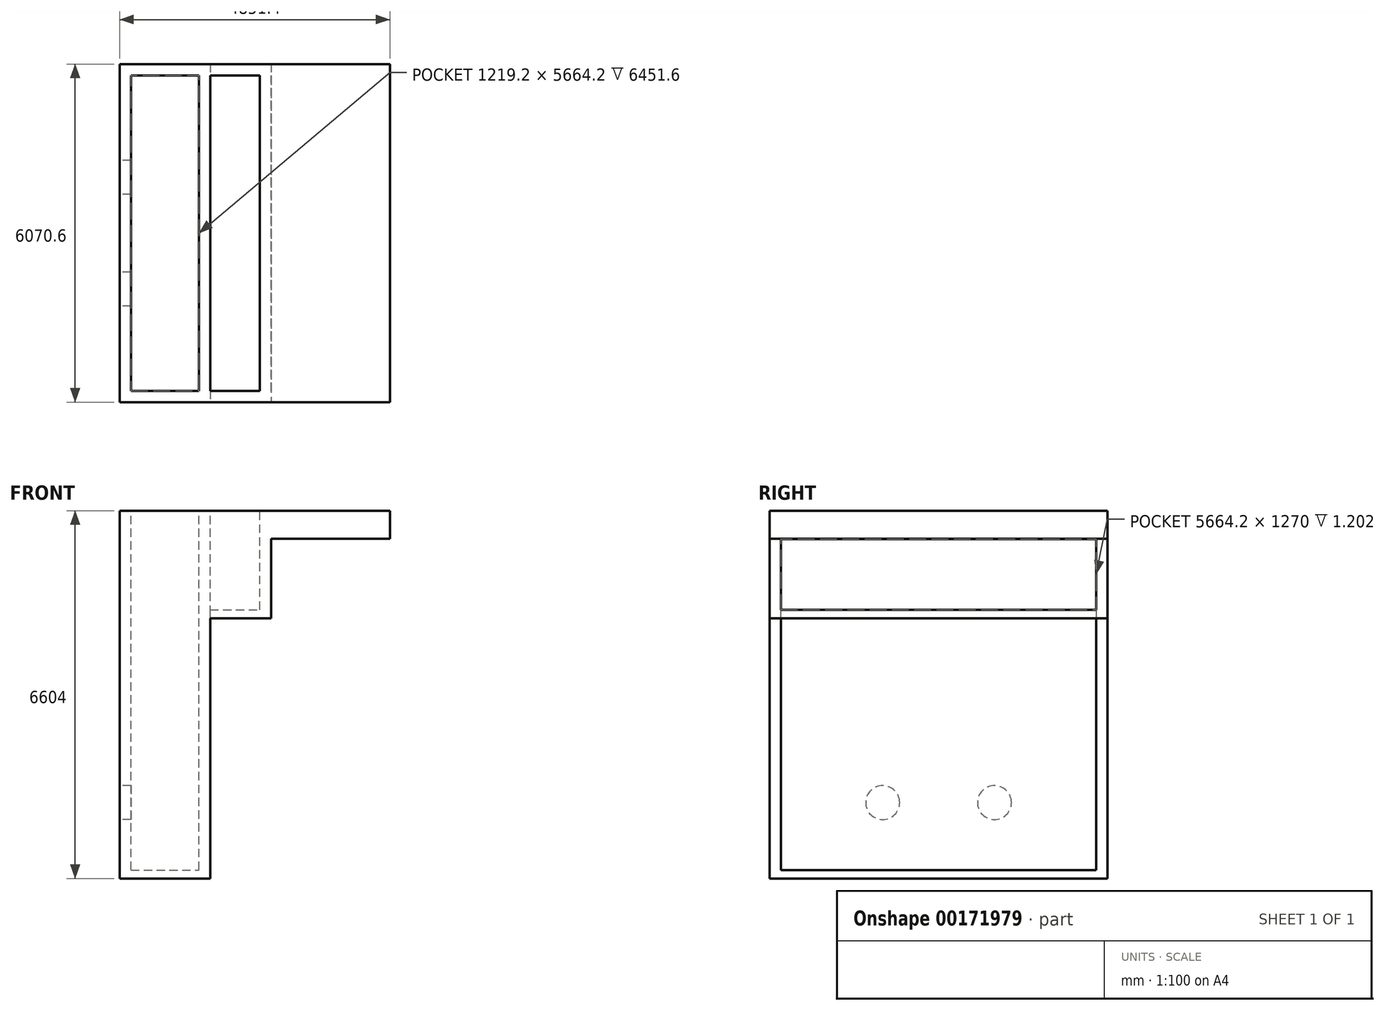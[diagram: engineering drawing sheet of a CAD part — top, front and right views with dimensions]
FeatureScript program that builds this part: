
annotation { "Feature Type Name" : "Feature", "Feature Type Description" : "" }
export const myFeature = defineFeature(function(context is Context, id is Id, definition is map)
    precondition{}
    {
        {
            var Q0;
            Q0=qCreatedBy(makeId("Top.planeOp"),FACE);
            var sketch = newSketch(context, id + "F0", { "sketchPlane" : qUnion([Q0])});
            skLineSegment(sketch, "E0.bottom", {"start": v(2222.5, 2832.1) * mm, "end": v(-2222.5, 2832.1) * mm});
            skLineSegment(sketch, "E0.top", {"start": v(2222.5, -2832.1) * mm, "end": v(-2222.5, -2832.1) * mm});
            skLineSegment(sketch, "E0.left", {"start": v(2222.5, 2832.1) * mm, "end": v(2222.5, -2832.1) * mm});
            skLineSegment(sketch, "E0.right", {"start": v(-2222.5, 2832.1) * mm, "end": v(-2222.5, -2832.1) * mm});
            skPoint(sketch, "E0.middle", {"position": v(0, 0) * mm});
            skSolve(sketch);
        }
        {
            var Q0;
            Q0=makeQuery(id+"F0.imprint","IMPRINT",FACE,{"disambiguationData":[TD([[makeQuery(id+"F0.imprint","IMPRINT",EDGE,{"derivedFrom":sQuery(id+"F0.wireOp",EDGE,"E0.bottom")}),1.0]])]});
            extrude(context, id + "F1", {"entities" : qUnion([Q0]), "oppositeDirection" : true, "depth" : 508 * mm});
        }
        {
            var Q0;
            Q0=makeQuery(id+"F1.opExtrude","CAP_FACE",FACE,{"disambiguationData":[OSD([sQuery(id+"F0.wireOp",EDGE,"E0.bottom"),sQuery(id+"F0.wireOp",EDGE,"E0.top"),sQuery(id+"F0.wireOp",EDGE,"E0.left"),sQuery(id+"F0.wireOp",EDGE,"E0.right")])],"isStart":true});
            var sketch = newSketch(context, id + "F2", { "sketchPlane" : qUnion([Q0])});
            skLineSegment(sketch, "E1.bottom", {"start": v(-2222.5, 2832.1) * mm, "end": v(-1003.3, 2832.1) * mm});
            skLineSegment(sketch, "E1.top", {"start": v(-2222.5, -2832.1) * mm, "end": v(-1003.3, -2832.1) * mm});
            skLineSegment(sketch, "E1.left", {"start": v(-2222.5, 2832.1) * mm, "end": v(-2222.5, -2832.1) * mm});
            skLineSegment(sketch, "E1.right", {"start": v(-1003.3, 2832.1) * mm, "end": v(-1003.3, -2832.1) * mm});
            skLineSegment(sketch, "E2.bottom", {"start": v(-1003.3, 2832.1) * mm, "end": v(-800.1, 2832.1) * mm});
            skLineSegment(sketch, "E2.top", {"start": v(-1003.3, -2832.1) * mm, "end": v(-800.1, -2832.1) * mm});
            skLineSegment(sketch, "E2.right", {"start": v(-800.1, 2832.1) * mm, "end": v(-800.1, -2832.1) * mm});
            skLineSegment(sketch, "E3.bottom", {"start": v(-800.1, 2832.1) * mm, "end": v(88.9, 2832.1) * mm});
            skLineSegment(sketch, "E3.top", {"start": v(-800.1, -2832.1) * mm, "end": v(88.9, -2832.1) * mm});
            skLineSegment(sketch, "E3.right", {"start": v(88.9, 2832.1) * mm, "end": v(88.9, -2832.1) * mm});
            skSolve(sketch);
        }
        {
            var Q0;
            Q0=makeQuery(id+"F2.imprint","IMPRINT",FACE,{"disambiguationData":[TD([[makeQuery(id+"F2.imprint","IMPRINT",EDGE,{"derivedFrom":sQuery(id+"F2.wireOp",EDGE,"E1.bottom")}),1.0]])]});
            var Q1;
            Q1=makeQuery(id+"F2.imprint","IMPRINT",FACE,{"disambiguationData":[TD([[makeQuery(id+"F2.imprint","IMPRINT",EDGE,{"derivedFrom":sQuery(id+"F2.wireOp",EDGE,"E3.bottom")}),1.0]])]});
            extrude(context, id + "F3", {"entities" : qUnion([Q0, Q1]), "operationType" : NewBodyOperationType.REMOVE, "oppositeDirection" : true, "depth" : 609.6 * mm});
        }
        {
            var Q0;
            Q0=makeQuery(id+"F1.opExtrude","CAP_FACE",FACE,{"disambiguationData":[OSD([sQuery(id+"F0.wireOp",EDGE,"E0.bottom"),sQuery(id+"F0.wireOp",EDGE,"E0.top"),sQuery(id+"F0.wireOp",EDGE,"E0.left"),sQuery(id+"F0.wireOp",EDGE,"E0.right")])],"isStart":false});
            var sketch = newSketch(context, id + "F4", { "sketchPlane" : qUnion([Q0])});
            skLineSegment(sketch, "E4.bottom", {"start": v(-2222.5, 2832.1) * mm, "end": v(2222.5, 2832.1) * mm});
            skLineSegment(sketch, "E4.top", {"start": v(-2222.5, -2832.1) * mm, "end": v(2222.5, -2832.1) * mm});
            skLineSegment(sketch, "E4.left", {"start": v(-2222.5, 2832.1) * mm, "end": v(-2222.5, -2832.1) * mm});
            skLineSegment(sketch, "E4.right", {"start": v(2222.5, 2832.1) * mm, "end": v(2222.5, -2832.1) * mm});
            skPoint(sketch, "E4.middle", {"position": v(0, 0) * mm});
            skLineSegment(sketch, "E5.bottom", {"start": v(-2425.7, 3035.3) * mm, "end": v(2425.7, 3035.3) * mm});
            skLineSegment(sketch, "E5.top", {"start": v(-2425.7, -3035.3) * mm, "end": v(2425.7, -3035.3) * mm});
            skLineSegment(sketch, "E5.left", {"start": v(-2425.7, 3035.3) * mm, "end": v(-2425.7, -3035.3) * mm});
            skLineSegment(sketch, "E5.right", {"start": v(2425.7, 3035.3) * mm, "end": v(2425.7, -3035.3) * mm});
            skSolve(sketch);
        }
        {
            var Q0;
            Q0 = qSketchRegion(id + "F4", true);
            extrude(context, id + "F5", {"entities" : qUnion([Q0]), "depth" : 6096 * mm});
        }
        {
            var Q0;
            Q0=makeQuery(id+"F5.opExtrude","CAP_FACE",FACE,{"disambiguationData":[OSD([sQuery(id+"F4.wireOp",EDGE,"E4.bottom"),sQuery(id+"F4.wireOp",EDGE,"E4.top"),sQuery(id+"F4.wireOp",EDGE,"E4.left"),sQuery(id+"F4.wireOp",EDGE,"E4.right"),sQuery(id+"F4.wireOp",EDGE,"E5.bottom"),sQuery(id+"F4.wireOp",EDGE,"E5.top"),sQuery(id+"F4.wireOp",EDGE,"E5.left"),sQuery(id+"F4.wireOp",EDGE,"E5.right")])],"isStart":true});
            extrude(context, id + "F6", {"entities" : qUnion([Q0]), "depth" : 508 * mm});
        }
        {
            var Q0;
            Q0=makeQuery(id+"F3.boolean.opBoolean","SPLIT",BODY,{"disambiguationData":[OD(0.0)],"derivedFrom":makeQuery(id+"F1.opExtrude","SWEPT_BODY",BODY,{"disambiguationData":[OSD([sQuery(id+"F0.wireOp",EDGE,"E0.bottom"),sQuery(id+"F0.wireOp",EDGE,"E0.top"),sQuery(id+"F0.wireOp",EDGE,"E0.left"),sQuery(id+"F0.wireOp",EDGE,"E0.right")])]})});
            var Q1;
            Q1=makeQuery(id+"F3.boolean.opBoolean","SPLIT",BODY,{"disambiguationData":[OD(1.0)],"derivedFrom":makeQuery(id+"F1.opExtrude","SWEPT_BODY",BODY,{"disambiguationData":[OSD([sQuery(id+"F0.wireOp",EDGE,"E0.bottom"),sQuery(id+"F0.wireOp",EDGE,"E0.top"),sQuery(id+"F0.wireOp",EDGE,"E0.left"),sQuery(id+"F0.wireOp",EDGE,"E0.right")])]})});
            var Q2;
            Q2=makeQuery(id+"F5.opExtrude","SWEPT_BODY",BODY,{"disambiguationData":[OSD([sQuery(id+"F4.wireOp",EDGE,"E4.bottom"),sQuery(id+"F4.wireOp",EDGE,"E4.top"),sQuery(id+"F4.wireOp",EDGE,"E4.left"),sQuery(id+"F4.wireOp",EDGE,"E4.right"),sQuery(id+"F4.wireOp",EDGE,"E5.bottom"),sQuery(id+"F4.wireOp",EDGE,"E5.top"),sQuery(id+"F4.wireOp",EDGE,"E5.left"),sQuery(id+"F4.wireOp",EDGE,"E5.right")])]});
            var Q3;
            Q3=makeQuery(id+"F6.opExtrude","SWEPT_BODY",BODY,{"disambiguationData":[OSD([sQuery(id+"F4.wireOp",EDGE,"E4.bottom"),sQuery(id+"F4.wireOp",EDGE,"E4.top"),sQuery(id+"F4.wireOp",EDGE,"E4.left"),sQuery(id+"F4.wireOp",EDGE,"E4.right"),sQuery(id+"F4.wireOp",EDGE,"E5.bottom"),sQuery(id+"F4.wireOp",EDGE,"E5.top"),sQuery(id+"F4.wireOp",EDGE,"E5.left"),sQuery(id+"F4.wireOp",EDGE,"E5.right")])]});
            booleanBodies(context, id + "F7", {"operationType" : BooleanOperationType.UNION, "tools" : qUnion([Q0, Q1, Q2, Q3])});
        }
        {
            var Q0;
            {var subQ0=sQuery(id+"F0.wireOp",EDGE,"E0.bottom");var subQ1=sQuery(id+"F0.wireOp",EDGE,"E0.top");Q0=makeQuery(id+"F3.boolean.opBoolean","SPLIT",FACE,{"disambiguationData":[TD([makeQuery(id+"F3.opExtrude","SWEPT_FACE",FACE,{"disambiguationData":[OSD([sQuery(id+"F2.wireOp",EDGE,"E1.right")])]})])],"derivedFrom":makeQuery(id+"F1.opExtrude","CAP_FACE",FACE,{"disambiguationData":[OSD([subQ0,subQ1,sQuery(id+"F0.wireOp",EDGE,"E0.left"),sQuery(id+"F0.wireOp",EDGE,"E0.right")])],"isStart":false})});}
            extrude(context, id + "F8", {"entities" : qUnion([Q0]), "operationType" : NewBodyOperationType.ADD, "depth" : 6096 * mm});
        }
        {
            var Q0;
            {var subQ0=sQuery(id+"F0.wireOp",EDGE,"E0.bottom");var subQ1=sQuery(id+"F0.wireOp",EDGE,"E0.top");var subQ2=sQuery(id+"F0.wireOp",EDGE,"E0.left");Q0=makeQuery(id+"F3.boolean.opBoolean","SPLIT",FACE,{"disambiguationData":[TD([makeQuery(id+"F1.opExtrude","SWEPT_FACE",FACE,{"disambiguationData":[OSD([subQ2])]})])],"derivedFrom":makeQuery(id+"F1.opExtrude","CAP_FACE",FACE,{"disambiguationData":[OSD([subQ0,subQ1,subQ2,sQuery(id+"F0.wireOp",EDGE,"E0.right")])],"isStart":false})});}
            var sketch = newSketch(context, id + "F9", { "sketchPlane" : qUnion([Q0])});
            skLineSegment(sketch, "E6.bottom", {"start": v(88.9, 2832.1) * mm, "end": v(292.1, 2832.1) * mm});
            skLineSegment(sketch, "E6.top", {"start": v(88.9, -2832.1) * mm, "end": v(292.1, -2832.1) * mm});
            skLineSegment(sketch, "E6.left", {"start": v(88.9, 2832.1) * mm, "end": v(88.9, -2832.1) * mm});
            skLineSegment(sketch, "E6.right", {"start": v(292.1, 2832.1) * mm, "end": v(292.1, -2832.1) * mm});
            skSolve(sketch);
        }
        {
            var Q0;
            Q0 = qSketchRegion(id + "F9", true);
            extrude(context, id + "F10", {"entities" : qUnion([Q0]), "operationType" : NewBodyOperationType.ADD, "depth" : 6096 * mm});
        }
        {
            var Q0;
            {var subQ0=sQuery(id+"F4.wireOp",EDGE,"E5.left");Q0=makeQuery(id+"F7.opBoolean","MERGE",FACE,{"derivedFrom":[makeQuery(id+"F5.opExtrude","SWEPT_FACE",FACE,{"disambiguationData":[OSD([subQ0])]}),makeQuery(id+"F6.opExtrude","SWEPT_FACE",FACE,{"disambiguationData":[OSD([subQ0])]})]});}
            var sketch = newSketch(context, id + "F11", { "sketchPlane" : qUnion([Q0])});
            skCircle(sketch, "E7", {"center": v(-1003.3, -5241.82) * mm, "radius": 304.8 * mm});
            skCircle(sketch, "E8", {"center": v(1003.3, -5241.82) * mm, "radius": 304.8 * mm});
            skSolve(sketch);
        }
        {
            var Q0;
            Q0 = qSketchRegion(id + "F11", true);
            extrude(context, id + "F12", {"entities" : qUnion([Q0]), "operationType" : NewBodyOperationType.REMOVE, "oppositeDirection" : true, "depth" : 203.2 * mm});
        }
        {
            var Q0;
            {var subQ0=sQuery(id+"F4.wireOp",EDGE,"E5.bottom");Q0=makeQuery(id+"F7.opBoolean","MERGE",FACE,{"derivedFrom":[makeQuery(id+"F5.opExtrude","SWEPT_FACE",FACE,{"disambiguationData":[OSD([subQ0])]}),makeQuery(id+"F6.opExtrude","SWEPT_FACE",FACE,{"disambiguationData":[OSD([subQ0])]})]});}
            var sketch = newSketch(context, id + "F13", { "sketchPlane" : qUnion([Q0])});
            skLineSegment(sketch, "E9", {"start": v(-799.73, -1930.4) * mm, "end": v(2425.7, -1930.4) * mm});
            skLineSegment(sketch, "E10", {"start": v(2425.7, -1930.4) * mm, "end": v(2425.7, -6604) * mm});
            skLineSegment(sketch, "E11", {"start": v(2425.7, -6604) * mm, "end": v(-799.73, -6604) * mm});
            skLineSegment(sketch, "E12", {"start": v(-799.73, -6604) * mm, "end": v(-799.73, -1930.4) * mm});
            skSolve(sketch);
        }
        {
            var Q0;
            Q0 = qSketchRegion(id + "F13", true);
            extrude(context, id + "F14", {"entities" : qUnion([Q0]), "operationType" : NewBodyOperationType.REMOVE, "endBound" : BoundingType.THROUGH_ALL, "oppositeDirection" : true, "depth" : 25.4 * mm});
        }
        {
            var Q0;
            {var subQ0=sQuery(id+"F4.wireOp",EDGE,"E5.bottom");Q0=makeQuery(id+"F7.opBoolean","MERGE",FACE,{"derivedFrom":[makeQuery(id+"F5.opExtrude","SWEPT_FACE",FACE,{"disambiguationData":[OSD([subQ0])]}),makeQuery(id+"F6.opExtrude","SWEPT_FACE",FACE,{"disambiguationData":[OSD([subQ0])]})]});}
            var sketch = newSketch(context, id + "F15", { "sketchPlane" : qUnion([Q0])});
            skLineSegment(sketch, "E13.bottom", {"start": v(293.3, -507.17) * mm, "end": v(2425.7, -507.17) * mm});
            skLineSegment(sketch, "E13.top", {"start": v(293.3, -1930.4) * mm, "end": v(2425.7, -1930.4) * mm});
            skLineSegment(sketch, "E13.left", {"start": v(293.3, -507.17) * mm, "end": v(293.3, -1930.4) * mm});
            skLineSegment(sketch, "E13.right", {"start": v(2425.7, -507.17) * mm, "end": v(2425.7, -1930.4) * mm});
            skSolve(sketch);
        }
        {
            var Q0;
            Q0 = qSketchRegion(id + "F15", true);
            extrude(context, id + "F16", {"entities" : qUnion([Q0]), "operationType" : NewBodyOperationType.REMOVE, "endBound" : BoundingType.THROUGH_ALL, "oppositeDirection" : true, "depth" : 25.4 * mm});
        }
        {
            var Q0;
            Q0=makeQuery(id+"F14.boolean.opBoolean","COPY",FACE,{"derivedFrom":makeQuery(id+"F14.opExtrude","SWEPT_FACE",FACE,{"disambiguationData":[OSD([sQuery(id+"F13.wireOp",EDGE,"E9")])]})});
            var sketch = newSketch(context, id + "F17", { "sketchPlane" : qUnion([Q0])});
            skLineSegment(sketch, "E14.bottom", {"start": v(293.3, -3035.3) * mm, "end": v(-799.73, -3035.3) * mm});
            skLineSegment(sketch, "E14.top", {"start": v(293.3, 3035.3) * mm, "end": v(-799.73, 3035.3) * mm});
            skLineSegment(sketch, "E14.left", {"start": v(293.3, -3035.3) * mm, "end": v(293.3, 3035.3) * mm});
            skLineSegment(sketch, "E14.right", {"start": v(-799.73, -3035.3) * mm, "end": v(-799.73, 3035.3) * mm});
            skSolve(sketch);
        }
        {
            var Q0;
            Q0=makeQuery(id+"F10.boolean.opBoolean","MERGE",FACE,{"derivedFrom":[makeQuery(id+"F8.boolean.opBoolean","MERGE",FACE,{"derivedFrom":[makeQuery(id+"F5.opExtrude","CAP_FACE",FACE,{"disambiguationData":[OSD([sQuery(id+"F4.wireOp",EDGE,"E4.bottom"),sQuery(id+"F4.wireOp",EDGE,"E4.top"),sQuery(id+"F4.wireOp",EDGE,"E4.left"),sQuery(id+"F4.wireOp",EDGE,"E4.right"),sQuery(id+"F4.wireOp",EDGE,"E5.bottom"),sQuery(id+"F4.wireOp",EDGE,"E5.top"),sQuery(id+"F4.wireOp",EDGE,"E5.left"),sQuery(id+"F4.wireOp",EDGE,"E5.right")])],"isStart":false}),makeQuery(id+"F8.opExtrude","CAP_FACE",FACE,{"disambiguationData":[OSD([sQuery(id+"F0.wireOp",EDGE,"E0.bottom"),sQuery(id+"F0.wireOp",EDGE,"E0.top"),sQuery(id+"F0.wireOp",EDGE,"E0.left"),sQuery(id+"F0.wireOp",EDGE,"E0.right")])],"isStart":false})]}),makeQuery(id+"F10.opExtrude","CAP_FACE",FACE,{"disambiguationData":[OSD([sQuery(id+"F9.wireOp",EDGE,"E6.bottom"),sQuery(id+"F9.wireOp",EDGE,"E6.top"),sQuery(id+"F9.wireOp",EDGE,"E6.left"),sQuery(id+"F9.wireOp",EDGE,"E6.right")])],"isStart":false})]});
            var sketch = newSketch(context, id + "F18", { "sketchPlane" : qUnion([Q0])});
            skLineSegment(sketch, "E15.bottom", {"start": v(-2425.7, 3035.3) * mm, "end": v(-799.73, 3035.3) * mm});
            skLineSegment(sketch, "E15.top", {"start": v(-2425.7, -3035.3) * mm, "end": v(-799.73, -3035.3) * mm});
            skLineSegment(sketch, "E15.left", {"start": v(-2425.7, 3035.3) * mm, "end": v(-2425.7, -3035.3) * mm});
            skLineSegment(sketch, "E15.right", {"start": v(-799.73, 3035.3) * mm, "end": v(-799.73, -3035.3) * mm});
            skSolve(sketch);
        }
        {
            var Q0;
            Q0 = qSketchRegion(id + "F18", true);
            extrude(context, id + "F19", {"entities" : qUnion([Q0]), "operationType" : NewBodyOperationType.ADD, "oppositeDirection" : true, "depth" : 152.4 * mm});
        }
        {
            var Q0;
            Q0 = qSketchRegion(id + "F17", true);
            extrude(context, id + "F20", {"entities" : qUnion([Q0]), "operationType" : NewBodyOperationType.ADD, "oppositeDirection" : true, "depth" : 152.4 * mm});
        }
    });
